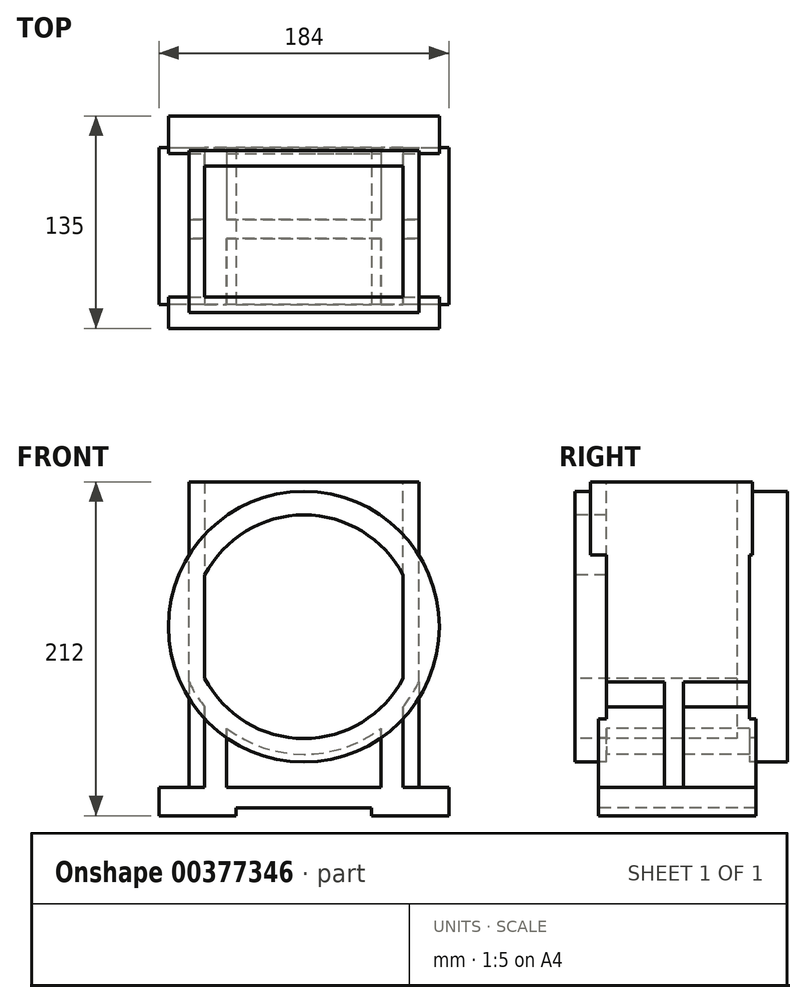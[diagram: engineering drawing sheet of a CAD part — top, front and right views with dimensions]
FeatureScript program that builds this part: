
annotation { "Feature Type Name" : "Feature", "Feature Type Description" : "" }
export const myFeature = defineFeature(function(context is Context, id is Id, definition is map)
    precondition{}
    {
        {
            var Q0;
            Q0=qCreatedBy(makeId("Top.planeOp"),FACE);
            var sketch = newSketch(context, id + "F0", { "sketchPlane" : qUnion([Q0])});
            skLineSegment(sketch, "E0", {"start": v(-92, 15) * mm, "end": v(-92, 115) * mm});
            skLineSegment(sketch, "E1", {"start": v(-92, 115) * mm, "end": v(92, 115) * mm});
            skLineSegment(sketch, "E2", {"start": v(92, 115) * mm, "end": v(92, 15) * mm});
            skLineSegment(sketch, "E3", {"start": v(92, 15) * mm, "end": v(-92, 15) * mm});
            skSolve(sketch);
        }
        {
            var Q0;
            Q0 = qSketchRegion(id + "F0", true);
            extrude(context, id + "F1", {"entities" : qUnion([Q0]), "depth" : 18 * mm});
        }
        {
            var Q0;
            Q0=makeQuery(id+"F1.opExtrude","SWEPT_FACE",FACE,{"disambiguationData":[OSD([sQuery(id+"F0.wireOp",EDGE,"E3")])]});
            var sketch = newSketch(context, id + "F2", { "sketchPlane" : qUnion([Q0])});
            skLineSegment(sketch, "E4.bottom", {"start": v(-43, 5) * mm, "end": v(43, 5) * mm});
            skLineSegment(sketch, "E4.top", {"start": v(-43, -16.71) * mm, "end": v(43, -16.71) * mm});
            skLineSegment(sketch, "E4.left", {"start": v(-43, 5) * mm, "end": v(-43, -16.71) * mm});
            skLineSegment(sketch, "E4.right", {"start": v(43, 5) * mm, "end": v(43, -16.71) * mm});
            skSolve(sketch);
        }
        {
            var Q0;
            Q0 = qSketchRegion(id + "F2", true);
            extrude(context, id + "F3", {"entities" : qUnion([Q0]), "operationType" : NewBodyOperationType.REMOVE, "endBound" : BoundingType.THROUGH_ALL, "oppositeDirection" : true, "depth" : 25 * mm});
        }
        {
            var Q0;
            Q0=makeQuery(id+"F1.opExtrude","CAP_FACE",FACE,{"disambiguationData":[OSD([sQuery(id+"F0.wireOp",EDGE,"E0"),sQuery(id+"F0.wireOp",EDGE,"E1"),sQuery(id+"F0.wireOp",EDGE,"E2"),sQuery(id+"F0.wireOp",EDGE,"E3")])],"isStart":false});
            var sketch = newSketch(context, id + "F4", { "sketchPlane" : qUnion([Q0])});
            skLineSegment(sketch, "E5", {"start": v(-63, 15) * mm, "end": v(-49, 15) * mm});
            skLineSegment(sketch, "E6", {"start": v(-49, 15) * mm, "end": v(-49, 57) * mm});
            skLineSegment(sketch, "E7", {"start": v(-49, 57) * mm, "end": v(0, 57) * mm});
            skLineSegment(sketch, "E8", {"start": v(-63, 15) * mm, "end": v(-63, 57) * mm});
            skLineSegment(sketch, "E9", {"start": v(-63, 57) * mm, "end": v(-73, 57) * mm});
            skLineSegment(sketch, "E10", {"start": v(-73, 57) * mm, "end": v(-73, 69) * mm});
            skLineSegment(sketch, "E11", {"start": v(-73, 69) * mm, "end": v(-63, 69) * mm});
            skLineSegment(sketch, "E12", {"start": v(-63, 69) * mm, "end": v(-63, 115) * mm});
            skLineSegment(sketch, "E13", {"start": v(-63, 115) * mm, "end": v(-49, 115) * mm});
            skLineSegment(sketch, "E14", {"start": v(-49, 115) * mm, "end": v(-49, 69) * mm});
            skLineSegment(sketch, "E15", {"start": v(-49, 69) * mm, "end": v(0, 69) * mm});
            skLineSegment(sketch, "E16.MirrorCS", {"start": v(63, 15) * mm, "end": v(49, 15) * mm});
            skLineSegment(sketch, "E17.MirrorCS", {"start": v(49, 15) * mm, "end": v(49, 57) * mm});
            skLineSegment(sketch, "E18.MirrorCS", {"start": v(63, 15) * mm, "end": v(63, 57) * mm});
            skLineSegment(sketch, "E19.MirrorCS", {"start": v(63, 57) * mm, "end": v(73, 57) * mm});
            skLineSegment(sketch, "E20.MirrorCS", {"start": v(73, 57) * mm, "end": v(73, 69) * mm});
            skLineSegment(sketch, "E21.MirrorCS", {"start": v(73, 69) * mm, "end": v(63, 69) * mm});
            skLineSegment(sketch, "E22.MirrorCS", {"start": v(63, 69) * mm, "end": v(63, 115) * mm});
            skLineSegment(sketch, "E23.MirrorCS", {"start": v(63, 115) * mm, "end": v(49, 115) * mm});
            skLineSegment(sketch, "E24.MirrorCS", {"start": v(49, 115) * mm, "end": v(49, 69) * mm});
            skLineSegment(sketch, "E25.MirrorCS", {"start": v(49, 69) * mm, "end": v(0, 69) * mm});
            skLineSegment(sketch, "E26.MirrorCS", {"start": v(49, 57) * mm, "end": v(0, 57) * mm});
            skSolve(sketch);
        }
        {
            var Q0;
            Q0 = qSketchRegion(id + "F4", true);
            extrude(context, id + "F5", {"entities" : qUnion([Q0]), "operationType" : NewBodyOperationType.ADD, "depth" : (110 - 18) * mm});
        }
        {
            var Q0;
            Q0=makeQuery(id+"F5.boolean.opBoolean","MERGE",FACE,{"derivedFrom":[makeQuery(id+"F1.opExtrude","SWEPT_FACE",FACE,{"disambiguationData":[OSD([sQuery(id+"F0.wireOp",EDGE,"E3")])]}),makeQuery(id+"F5.opExtrude","SWEPT_FACE",FACE,{"disambiguationData":[OSD([sQuery(id+"F4.wireOp",EDGE,"E5")])]}),makeQuery(id+"F5.opExtrude","SWEPT_FACE",FACE,{"disambiguationData":[OSD([sQuery(id+"F4.wireOp",EDGE,"E16.MirrorCS")])]})]});
            var sketch = newSketch(context, id + "F6", { "sketchPlane" : qUnion([Q0])});
            skArc(sketch, "E27", {"start": v(-73, 84.9) * mm, "mid": v(0, 39) * mm, "end": v(73, 84.9) * mm});
            skLineSegment(sketch, "E28", {"start": v(-73, 120) * mm, "end": v(73, 120) * mm});
            skLineSegment(sketch, "E29", {"start": v(73, 120) * mm, "end": v(73, 84.9) * mm});
            skLineSegment(sketch, "E30", {"start": v(-73, 120) * mm, "end": v(-73, 84.9) * mm});
            skSolve(sketch);
        }
        {
            var Q0;
            Q0 = qSketchRegion(id + "F6", true);
            extrude(context, id + "F7", {"entities" : qUnion([Q0]), "operationType" : NewBodyOperationType.ADD, "oppositeDirection" : true, "depth" : 100 * mm});
        }
        {
            var Q0;
            Q0=qCreatedBy(makeId("Front.planeOp"),FACE);
            var sketch = newSketch(context, id + "F8", { "sketchPlane" : qUnion([Q0])});
            skCircle(sketch, "E31", {"center": v(0, 120) * mm, "radius": 86 * mm});
            skSolve(sketch);
        }
        {
            var Q0;
            Q0 = qSketchRegion(id + "F8", true);
            extrude(context, id + "F9", {"entities" : qUnion([Q0]), "operationType" : NewBodyOperationType.ADD, "oppositeDirection" : true, "depth" : 20 * mm});
        }
        {
            var Q0;
            Q0 = qSketchRegion(id + "F8", true);
            extrude(context, id + "F10", {"entities" : qUnion([Q0]), "operationType" : NewBodyOperationType.ADD, "oppositeDirection" : true, "depth" : 135 * mm, "hasSecondDirection" : true, "secondDirectionOppositeDirection" : true, "secondDirectionDepth" : (135 - 24) * mm});
        }
        {
            var Q0;
            Q0=qCreatedBy(makeId("Top.planeOp"),FACE);
            cPlane(context, id + "F11", {"entities" : qUnion([Q0]), "cplaneType" : CPlaneType.OFFSET, "offset" : 212 * mm, "width" : 150 * mm, "height" : 150 * mm});
        }
        {
            var Q0;
            Q0=qCreatedBy(id+"F11.planeOp",FACE);
            var sketch = newSketch(context, id + "F12", { "sketchPlane" : qUnion([Q0])});
            skLineSegment(sketch, "E32.bottom", {"start": v(-73, 10) * mm, "end": v(73, 10) * mm});
            skLineSegment(sketch, "E32.top", {"start": v(-73, 113) * mm, "end": v(73, 113) * mm});
            skLineSegment(sketch, "E32.left", {"start": v(-73, 10) * mm, "end": v(-73, 113) * mm});
            skLineSegment(sketch, "E32.right", {"start": v(73, 10) * mm, "end": v(73, 113) * mm});
            skSolve(sketch);
        }
        {
            var Q0;
            Q0 = qSketchRegion(id + "F12", true);
            extrude(context, id + "F13", {"entities" : qUnion([Q0]), "operationType" : NewBodyOperationType.ADD, "endBound" : BoundingType.UP_TO_NEXT, "oppositeDirection" : true, "depth" : 25 * mm});
        }
        {
            var Q0;
            Q0=makeQuery(id+"F9.opExtrude","CAP_FACE",FACE,{"disambiguationData":[OSD([sQuery(id+"F8.wireOp",EDGE,"E31")])],"isStart":true});
            var sketch = newSketch(context, id + "F14", { "sketchPlane" : qUnion([Q0])});
            skArc(sketch, "E33", {"start": v(-63, 87.26) * mm, "mid": v(0, 49) * mm, "end": v(63, 87.26) * mm});
            skLineSegment(sketch, "E34", {"start": v(-63, 152.74) * mm, "end": v(-63, 87.26) * mm});
            skLineSegment(sketch, "E35.MirrorCS", {"start": v(63, 152.74) * mm, "end": v(63, 87.26) * mm});
            skArc(sketch, "E36.trimOffspring", {"start": v(63, 152.74) * mm, "mid": v(0, 191) * mm, "end": v(-63, 152.74) * mm});
            skSolve(sketch);
        }
        {
            var Q0;
            Q0 = qSketchRegion(id + "F14", true);
            extrude(context, id + "F15", {"entities" : qUnion([Q0]), "operationType" : NewBodyOperationType.REMOVE, "oppositeDirection" : true, "depth" : 103 * mm});
        }
        {
            var Q0;
            Q0=makeQuery(id+"F13.opExtrude","CAP_FACE",FACE,{"disambiguationData":[OSD([sQuery(id+"F12.wireOp",EDGE,"E32.bottom"),sQuery(id+"F12.wireOp",EDGE,"E32.top"),sQuery(id+"F12.wireOp",EDGE,"E32.left"),sQuery(id+"F12.wireOp",EDGE,"E32.right")])],"isStart":true});
            var sketch = newSketch(context, id + "F16", { "sketchPlane" : qUnion([Q0])});
            skLineSegment(sketch, "E37.bottom", {"start": v(-63, 20) * mm, "end": v(63, 20) * mm});
            skLineSegment(sketch, "E37.top", {"start": v(-63, 103) * mm, "end": v(63, 103) * mm});
            skLineSegment(sketch, "E37.left", {"start": v(-63, 20) * mm, "end": v(-63, 103) * mm});
            skLineSegment(sketch, "E37.right", {"start": v(63, 20) * mm, "end": v(63, 103) * mm});
            skSolve(sketch);
        }
        {
            var Q0;
            Q0 = qSketchRegion(id + "F16", true);
            extrude(context, id + "F17", {"entities" : qUnion([Q0]), "operationType" : NewBodyOperationType.REMOVE, "endBound" : BoundingType.UP_TO_NEXT, "oppositeDirection" : true, "depth" : 25 * mm});
        }
    });
